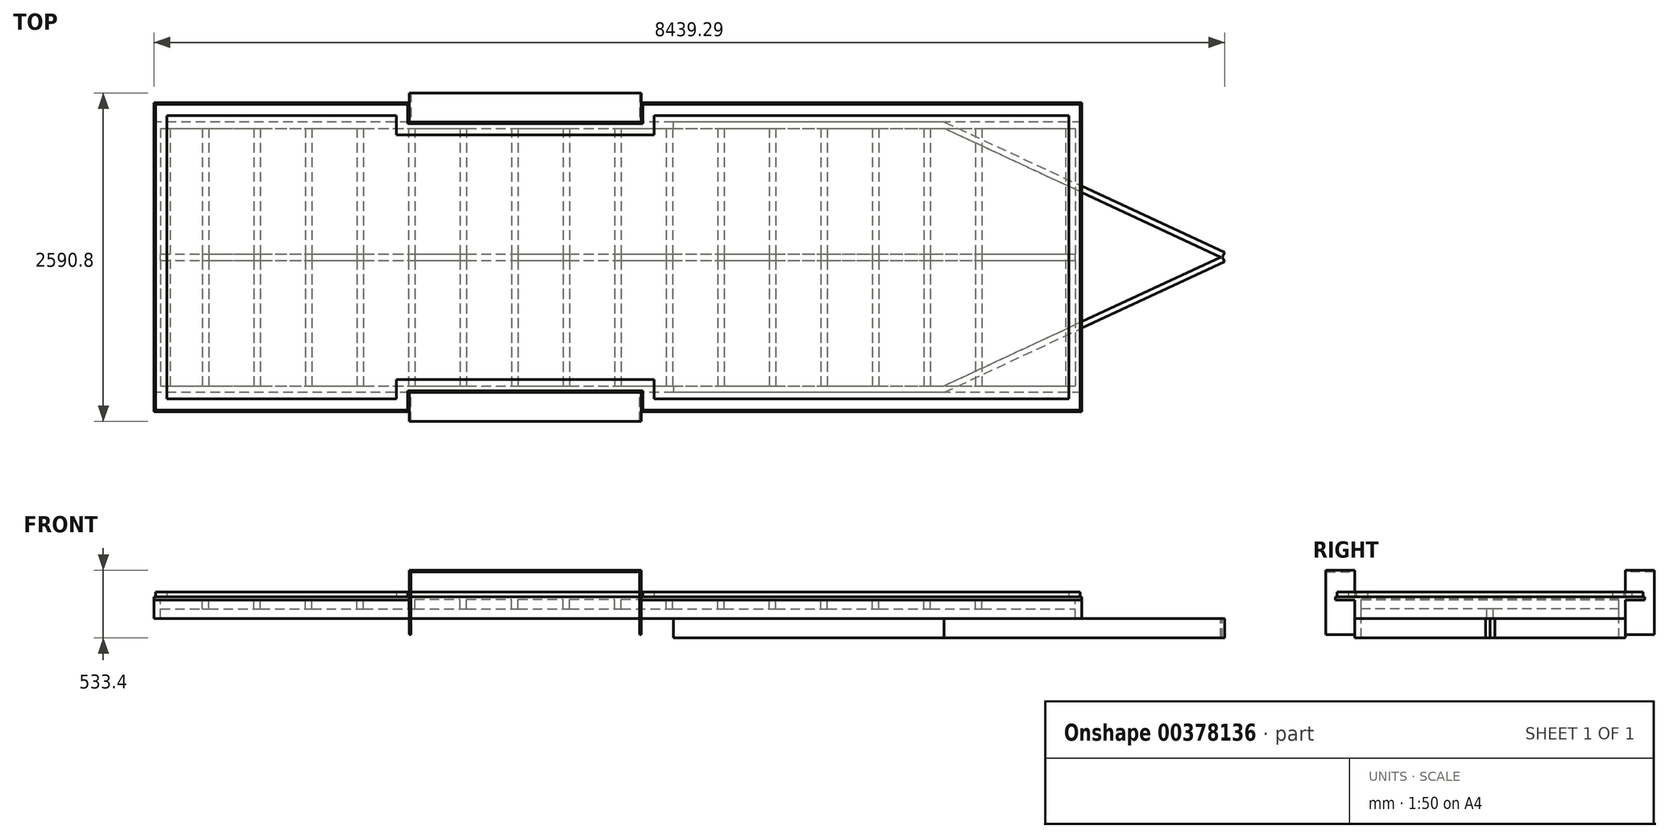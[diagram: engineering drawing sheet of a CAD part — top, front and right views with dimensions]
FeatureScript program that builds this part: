
annotation { "Feature Type Name" : "Feature", "Feature Type Description" : "" }
export const myFeature = defineFeature(function(context is Context, id is Id, definition is map)
    precondition{}
    {
        {
            var Q0;
            Q0=qCreatedBy(makeId("Top.planeOp"),FACE);
            var sketch = newSketch(context, id + "F0", { "sketchPlane" : qUnion([Q0])});
            skLineSegment(sketch, "E0.bottom", {"start": v(3657.6, 1219.2) * mm, "end": v(184.15, 1219.2) * mm});
            skLineSegment(sketch, "E0.top", {"start": v(3657.6, -1219.2) * mm, "end": v(184.15, -1219.2) * mm});
            skLineSegment(sketch, "E0.left", {"start": v(3657.6, 1219.2) * mm, "end": v(3657.6, -1219.2) * mm});
            skLineSegment(sketch, "E0.right", {"start": v(-3657.6, 1219.2) * mm, "end": v(-3657.6, -1219.2) * mm});
            skPoint(sketch, "E0.middle", {"position": v(0, 0) * mm});
            skLineSegment(sketch, "E1.bottom", {"start": v(3657.6, 1066.8) * mm, "end": v(-3657.6, 1066.8) * mm});
            skLineSegment(sketch, "E1.top", {"start": v(3657.6, -1066.8) * mm, "end": v(-3657.6, -1066.8) * mm});
            skLineSegment(sketch, "E2.bottom", {"start": v(-3606.8, 1016) * mm, "end": v(3606.8, 1016) * mm});
            skLineSegment(sketch, "E2.top", {"start": v(-3606.8, -1016) * mm, "end": v(3606.8, -1016) * mm});
            skLineSegment(sketch, "E2.left", {"start": v(-3606.8, 1016) * mm, "end": v(-3606.8, -1016) * mm});
            skLineSegment(sketch, "E2.right", {"start": v(3606.8, 1016) * mm, "end": v(3606.8, -1016) * mm});
            skLineSegment(sketch, "E3", {"start": v(-3530.6, 1016) * mm, "end": v(-3530.6, -1016) * mm});
            skLineSegment(sketch, "E4", {"start": v(3530.6, 1016) * mm, "end": v(3530.6, -1016) * mm});
            skLineSegment(sketch, "E5", {"start": v(3251.2, 1016) * mm, "end": v(3251.2, -1016) * mm, "construction": true});
            skPoint(sketch, "E6", {"position": v(3251.2, 0) * mm});
            skLineSegment(sketch, "E7.bottom", {"start": v(3276.6, 1016) * mm, "end": v(3225.8, 1016) * mm});
            skLineSegment(sketch, "E7.top", {"start": v(3276.6, -1016) * mm, "end": v(3225.8, -1016) * mm});
            skLineSegment(sketch, "E7.left", {"start": v(3276.6, 1016) * mm, "end": v(3276.6, -1016) * mm});
            skLineSegment(sketch, "E7.right", {"start": v(3225.8, 1016) * mm, "end": v(3225.8, -1016) * mm});
            skLineSegment(sketch, "E8.1.0.0", {"start": v(2819.4, 1016) * mm, "end": v(2819.4, -1016) * mm});
            skLineSegment(sketch, "E8.1.0.1", {"start": v(2870.2, 1016) * mm, "end": v(2870.2, -1016) * mm});
            skLineSegment(sketch, "E8.2.0.0", {"start": v(2413, 1016) * mm, "end": v(2413, -1016) * mm});
            skLineSegment(sketch, "E8.2.0.1", {"start": v(2463.8, 1016) * mm, "end": v(2463.8, -1016) * mm});
            skLineSegment(sketch, "E8.3.0.0", {"start": v(2006.6, 1016) * mm, "end": v(2006.6, -1016) * mm});
            skLineSegment(sketch, "E8.3.0.1", {"start": v(2057.4, 1016) * mm, "end": v(2057.4, -1016) * mm});
            skLineSegment(sketch, "E8.4.0.0", {"start": v(1600.2, 1016) * mm, "end": v(1600.2, -1016) * mm});
            skLineSegment(sketch, "E8.4.0.1", {"start": v(1651, 1016) * mm, "end": v(1651, -1016) * mm});
            skLineSegment(sketch, "E8.5.0.0", {"start": v(1193.8, 1016) * mm, "end": v(1193.8, -1016) * mm});
            skLineSegment(sketch, "E8.5.0.1", {"start": v(1244.6, 1016) * mm, "end": v(1244.6, -1016) * mm});
            skLineSegment(sketch, "E8.6.0.0", {"start": v(787.4, 1016) * mm, "end": v(787.4, -1016) * mm});
            skLineSegment(sketch, "E8.6.0.1", {"start": v(838.2, 1016) * mm, "end": v(838.2, -1016) * mm});
            skLineSegment(sketch, "E8.7.0.0", {"start": v(381, 1016) * mm, "end": v(381, -1016) * mm});
            skLineSegment(sketch, "E8.7.0.1", {"start": v(431.8, 1016) * mm, "end": v(431.8, -1016) * mm});
            skLineSegment(sketch, "E8.8.0.0", {"start": v(-25.4, 1016) * mm, "end": v(-25.4, -1016) * mm});
            skLineSegment(sketch, "E8.8.0.1", {"start": v(25.4, 1016) * mm, "end": v(25.4, -1016) * mm});
            skLineSegment(sketch, "E8.9.0.0", {"start": v(-431.8, 1016) * mm, "end": v(-431.8, -1016) * mm});
            skLineSegment(sketch, "E8.9.0.1", {"start": v(-381, 1016) * mm, "end": v(-381, -1016) * mm});
            skLineSegment(sketch, "E8.10.0.0", {"start": v(-838.2, 1016) * mm, "end": v(-838.2, -1016) * mm});
            skLineSegment(sketch, "E8.10.0.1", {"start": v(-787.4, 1016) * mm, "end": v(-787.4, -1016) * mm});
            skLineSegment(sketch, "E8.11.0.0", {"start": v(-1244.6, 1016) * mm, "end": v(-1244.6, -1016) * mm});
            skLineSegment(sketch, "E8.11.0.1", {"start": v(-1193.8, 1016) * mm, "end": v(-1193.8, -1016) * mm});
            skLineSegment(sketch, "E8.12.0.0", {"start": v(-1651, 1016) * mm, "end": v(-1651, -1016) * mm});
            skLineSegment(sketch, "E8.12.0.1", {"start": v(-1600.2, 1016) * mm, "end": v(-1600.2, -1016) * mm});
            skLineSegment(sketch, "E8.13.0.0", {"start": v(-2057.4, 1016) * mm, "end": v(-2057.4, -1016) * mm});
            skLineSegment(sketch, "E8.13.0.1", {"start": v(-2006.6, 1016) * mm, "end": v(-2006.6, -1016) * mm});
            skLineSegment(sketch, "E8.14.0.0", {"start": v(-2463.8, 1016) * mm, "end": v(-2463.8, -1016) * mm});
            skLineSegment(sketch, "E8.14.0.1", {"start": v(-2413, 1016) * mm, "end": v(-2413, -1016) * mm});
            skLineSegment(sketch, "E8.15.0.0", {"start": v(-2870.2, 1016) * mm, "end": v(-2870.2, -1016) * mm});
            skLineSegment(sketch, "E8.15.0.1", {"start": v(-2819.4, 1016) * mm, "end": v(-2819.4, -1016) * mm});
            skLineSegment(sketch, "E8.16.0.0", {"start": v(-3276.6, 1016) * mm, "end": v(-3276.6, -1016) * mm});
            skLineSegment(sketch, "E8.16.0.1", {"start": v(-3225.8, 1016) * mm, "end": v(-3225.8, -1016) * mm});
            skLineSegment(sketch, "E8.direction1", {"start": v(3225.8, -1016) * mm, "end": v(2819.4, -1016) * mm, "construction": true});
            skLineSegment(sketch, "E9", {"start": v(-1644.65, 1219.2) * mm, "end": v(-1644.65, 1066.8) * mm});
            skLineSegment(sketch, "E10", {"start": v(184.15, 1219.2) * mm, "end": v(184.15, 1066.8) * mm});
            skLineSegment(sketch, "E11", {"start": v(184.15, -1066.8) * mm, "end": v(184.15, -1219.2) * mm});
            skLineSegment(sketch, "E12", {"start": v(-1644.65, -1066.8) * mm, "end": v(-1644.65, -1219.2) * mm});
            skLineSegment(sketch, "E13.trimOffspring", {"start": v(-1644.65, 1219.2) * mm, "end": v(-3657.6, 1219.2) * mm});
            skLineSegment(sketch, "E14.trimOffspring", {"start": v(-1644.65, -1219.2) * mm, "end": v(-3657.6, -1219.2) * mm});
            skSolve(sketch);
        }
        {
            var Q0;
            {var subQ4=sQuery(id+"F0.wireOp",EDGE,"E12");Q0=makeQuery(id+"F0.imprint","IMPRINT",FACE,{"disambiguationData":[TD([[makeQuery(id+"F0.imprint","IMPRINT",EDGE,{"derivedFrom":subQ4}),-1.0]])]});}
            var Q1;
            {var subQ0=sQuery(id+"F0.wireOp",EDGE,"E2.left");Q1=makeQuery(id+"F0.imprint","IMPRINT",FACE,{"disambiguationData":[TD([[makeQuery(id+"F0.imprint","IMPRINT",EDGE,{"derivedFrom":subQ0}),1.0]])]});}
            var Q2;
            {var subQ4=sQuery(id+"F0.wireOp",EDGE,"E9");Q2=makeQuery(id+"F0.imprint","IMPRINT",FACE,{"disambiguationData":[TD([[makeQuery(id+"F0.imprint","IMPRINT",EDGE,{"derivedFrom":subQ4}),-1.0]])]});}
            var Q3;
            {var subQ0=sQuery(id+"F0.wireOp",EDGE,"E0.bottom");Q3=makeQuery(id+"F0.imprint","IMPRINT",FACE,{"disambiguationData":[TD([[makeQuery(id+"F0.imprint","IMPRINT",EDGE,{"derivedFrom":subQ0}),1.0]])]});}
            var Q4;
            {var subQ0=sQuery(id+"F0.wireOp",EDGE,"E2.right");Q4=makeQuery(id+"F0.imprint","IMPRINT",FACE,{"disambiguationData":[TD([[makeQuery(id+"F0.imprint","IMPRINT",EDGE,{"derivedFrom":subQ0}),-1.0]])]});}
            var Q5;
            {var subQ0=sQuery(id+"F0.wireOp",EDGE,"E0.top");Q5=makeQuery(id+"F0.imprint","IMPRINT",FACE,{"disambiguationData":[TD([[makeQuery(id+"F0.imprint","IMPRINT",EDGE,{"derivedFrom":subQ0}),-1.0]])]});}
            extrude(context, id + "F1", {"entities" : qUnion([Q0, Q1, Q2, Q3, Q4, Q5]), "oppositeDirection" : true, "depth" : 6.35 * mm});
        }
        {
            var Q0;
            {var subQ64=sQuery(id+"F0.wireOp",EDGE,"E2.left");Q0=makeQuery(id+"F0.imprint","IMPRINT",FACE,{"disambiguationData":[TD([[makeQuery(id+"F0.imprint","IMPRINT",EDGE,{"derivedFrom":subQ64}),-1.0]])]});}
            extrude(context, id + "F2", {"entities" : qUnion([Q0]), "oppositeDirection" : true, "depth" : 152.4 * mm});
        }
        {
            var Q0;
            {var subQ0=sQuery(id+"F0.wireOp",EDGE,"E8.16.0.0");Q0=makeQuery(id+"F0.imprint","IMPRINT",FACE,{"disambiguationData":[TD([[makeQuery(id+"F0.imprint","IMPRINT",EDGE,{"derivedFrom":subQ0}),1.0]])]});}
            var Q1;
            {var subQ0=sQuery(id+"F0.wireOp",EDGE,"E8.15.0.0");Q1=makeQuery(id+"F0.imprint","IMPRINT",FACE,{"disambiguationData":[TD([[makeQuery(id+"F0.imprint","IMPRINT",EDGE,{"derivedFrom":subQ0}),1.0]])]});}
            var Q2;
            {var subQ0=sQuery(id+"F0.wireOp",EDGE,"E8.14.0.0");Q2=makeQuery(id+"F0.imprint","IMPRINT",FACE,{"disambiguationData":[TD([[makeQuery(id+"F0.imprint","IMPRINT",EDGE,{"derivedFrom":subQ0}),1.0]])]});}
            var Q3;
            {var subQ0=sQuery(id+"F0.wireOp",EDGE,"E8.13.0.0");Q3=makeQuery(id+"F0.imprint","IMPRINT",FACE,{"disambiguationData":[TD([[makeQuery(id+"F0.imprint","IMPRINT",EDGE,{"derivedFrom":subQ0}),1.0]])]});}
            var Q4;
            {var subQ0=sQuery(id+"F0.wireOp",EDGE,"E8.12.0.0");Q4=makeQuery(id+"F0.imprint","IMPRINT",FACE,{"disambiguationData":[TD([[makeQuery(id+"F0.imprint","IMPRINT",EDGE,{"derivedFrom":subQ0}),1.0]])]});}
            var Q5;
            {var subQ0=sQuery(id+"F0.wireOp",EDGE,"E8.11.0.0");Q5=makeQuery(id+"F0.imprint","IMPRINT",FACE,{"disambiguationData":[TD([[makeQuery(id+"F0.imprint","IMPRINT",EDGE,{"derivedFrom":subQ0}),1.0]])]});}
            var Q6;
            {var subQ0=sQuery(id+"F0.wireOp",EDGE,"E8.10.0.0");Q6=makeQuery(id+"F0.imprint","IMPRINT",FACE,{"disambiguationData":[TD([[makeQuery(id+"F0.imprint","IMPRINT",EDGE,{"derivedFrom":subQ0}),1.0]])]});}
            var Q7;
            {var subQ0=sQuery(id+"F0.wireOp",EDGE,"E8.9.0.0");Q7=makeQuery(id+"F0.imprint","IMPRINT",FACE,{"disambiguationData":[TD([[makeQuery(id+"F0.imprint","IMPRINT",EDGE,{"derivedFrom":subQ0}),1.0]])]});}
            var Q8;
            {var subQ0=sQuery(id+"F0.wireOp",EDGE,"E8.8.0.0");Q8=makeQuery(id+"F0.imprint","IMPRINT",FACE,{"disambiguationData":[TD([[makeQuery(id+"F0.imprint","IMPRINT",EDGE,{"derivedFrom":subQ0}),1.0]])]});}
            var Q9;
            {var subQ0=sQuery(id+"F0.wireOp",EDGE,"E8.7.0.0");Q9=makeQuery(id+"F0.imprint","IMPRINT",FACE,{"disambiguationData":[TD([[makeQuery(id+"F0.imprint","IMPRINT",EDGE,{"derivedFrom":subQ0}),1.0]])]});}
            var Q10;
            {var subQ0=sQuery(id+"F0.wireOp",EDGE,"E8.6.0.0");Q10=makeQuery(id+"F0.imprint","IMPRINT",FACE,{"disambiguationData":[TD([[makeQuery(id+"F0.imprint","IMPRINT",EDGE,{"derivedFrom":subQ0}),1.0]])]});}
            var Q11;
            {var subQ0=sQuery(id+"F0.wireOp",EDGE,"E8.5.0.0");Q11=makeQuery(id+"F0.imprint","IMPRINT",FACE,{"disambiguationData":[TD([[makeQuery(id+"F0.imprint","IMPRINT",EDGE,{"derivedFrom":subQ0}),1.0]])]});}
            var Q12;
            {var subQ0=sQuery(id+"F0.wireOp",EDGE,"E8.4.0.0");Q12=makeQuery(id+"F0.imprint","IMPRINT",FACE,{"disambiguationData":[TD([[makeQuery(id+"F0.imprint","IMPRINT",EDGE,{"derivedFrom":subQ0}),1.0]])]});}
            var Q13;
            {var subQ0=sQuery(id+"F0.wireOp",EDGE,"E8.3.0.0");Q13=makeQuery(id+"F0.imprint","IMPRINT",FACE,{"disambiguationData":[TD([[makeQuery(id+"F0.imprint","IMPRINT",EDGE,{"derivedFrom":subQ0}),1.0]])]});}
            var Q14;
            {var subQ0=sQuery(id+"F0.wireOp",EDGE,"E8.2.0.0");Q14=makeQuery(id+"F0.imprint","IMPRINT",FACE,{"disambiguationData":[TD([[makeQuery(id+"F0.imprint","IMPRINT",EDGE,{"derivedFrom":subQ0}),1.0]])]});}
            var Q15;
            {var subQ0=sQuery(id+"F0.wireOp",EDGE,"E8.1.0.0");Q15=makeQuery(id+"F0.imprint","IMPRINT",FACE,{"disambiguationData":[TD([[makeQuery(id+"F0.imprint","IMPRINT",EDGE,{"derivedFrom":subQ0}),1.0]])]});}
            var Q16;
            Q16=makeQuery(id+"F0.imprint","IMPRINT",FACE,{"disambiguationData":[TD([[makeQuery(id+"F0.imprint","IMPRINT",EDGE,{"derivedFrom":sQuery(id+"F0.wireOp",EDGE,"E7.bottom")}),1.0]])]});
            extrude(context, id + "F3", {"entities" : qUnion([Q0, Q1, Q2, Q3, Q4, Q5, Q6, Q7, Q8, Q9, Q10, Q11, Q12, Q13, Q14, Q15, Q16]), "oppositeDirection" : true, "depth" : 76.2 * mm});
        }
        {
            var Q0;
            Q0=makeQuery(id+"F3.opExtrude","CAP_FACE",FACE,{"disambiguationData":[OSD([sQuery(id+"F0.wireOp",EDGE,"E2.bottom"),sQuery(id+"F0.wireOp",EDGE,"E2.top"),sQuery(id+"F0.wireOp",EDGE,"E8.10.0.0"),sQuery(id+"F0.wireOp",EDGE,"E8.10.0.1")])],"isStart":false});
            var sketch = newSketch(context, id + "F4", { "sketchPlane" : qUnion([Q0])});
            skLineSegment(sketch, "E15.bottom", {"start": v(-3606.8, 25.4) * mm, "end": v(3606.8, 25.4) * mm});
            skLineSegment(sketch, "E15.top", {"start": v(-3606.8, -25.4) * mm, "end": v(3606.8, -25.4) * mm});
            skLineSegment(sketch, "E15.left", {"start": v(-3606.8, 25.4) * mm, "end": v(-3606.8, -25.4) * mm});
            skLineSegment(sketch, "E15.right", {"start": v(3606.8, 25.4) * mm, "end": v(3606.8, -25.4) * mm});
            skPoint(sketch, "E15.middle", {"position": v(0, 0) * mm});
            skSolve(sketch);
        }
        {
            var Q0;
            {var subQ0=sQuery(id+"F4.wireOp",EDGE,"E15.left");Q0=makeQuery(id+"F4.imprint","IMPRINT",FACE,{"disambiguationData":[TD([[makeQuery(id+"F4.imprint","IMPRINT",EDGE,{"derivedFrom":subQ0}),1.0]])]});}
            var Q1;
            {var subQ0=sQuery(id+"F4.wireOp",EDGE,"E15.right");Q1=makeQuery(id+"F4.imprint","IMPRINT",FACE,{"disambiguationData":[TD([[makeQuery(id+"F4.imprint","IMPRINT",EDGE,{"derivedFrom":subQ0}),-1.0]])]});}
            var Q2;
            {var subQ0=sQuery(id+"F4.wireOp",EDGE,"E15.bottom");var subQ1=makeQuery(id+"F3.opExtrude","CAP_EDGE",EDGE,{"disambiguationData":[OSD([sQuery(id+"F0.wireOp",EDGE,"E8.10.0.0")])],"isStart":false});var subQ2=makeQuery(id+"F4.imprint","INTERSECT",VERTEX,{"derivedFrom":[subQ1,subQ0]});Q2=makeQuery(id+"F4.imprint","IMPRINT",FACE,{"disambiguationData":[TD([[makeQuery(id+"F4.imprint","IMPRINT",EDGE,{"disambiguationData":[TD([[subQ2,-1.0]])],"derivedFrom":subQ0}),-1.0]])]});}
            extrude(context, id + "F5", {"entities" : qUnion([Q0, Q1, Q2]), "operationType" : NewBodyOperationType.ADD, "depth" : 76.2 * mm});
        }
        {
            var Q0;
            Q0=makeQuery(id+"F2.opExtrude","SWEPT_FACE",FACE,{"disambiguationData":[OSD([sQuery(id+"F0.wireOp",EDGE,"E1.top")])]});
            var sketch = newSketch(context, id + "F6", { "sketchPlane" : qUnion([Q0])});
            skLineSegment(sketch, "E16", {"start": v(-1644.65, -279.4) * mm, "end": v(-1644.65, 228.6) * mm});
            skLineSegment(sketch, "E17", {"start": v(-1644.65, 228.6) * mm, "end": v(184.15, 228.6) * mm});
            skLineSegment(sketch, "E18", {"start": v(184.15, 228.6) * mm, "end": v(184.15, -279.4) * mm});
            skLineSegment(sketch, "E19.0", {"start": v(171.45, 215.9) * mm, "end": v(171.45, -279.4) * mm});
            skLineSegment(sketch, "E19.1", {"start": v(-1631.95, 215.9) * mm, "end": v(171.45, 215.9) * mm});
            skLineSegment(sketch, "E19.2", {"start": v(-1631.95, -279.4) * mm, "end": v(-1631.95, 215.9) * mm});
            skLineSegment(sketch, "E20", {"start": v(-1644.65, -279.4) * mm, "end": v(-1631.95, -279.4) * mm});
            skLineSegment(sketch, "E21", {"start": v(171.45, -279.4) * mm, "end": v(184.15, -279.4) * mm});
            skSolve(sketch);
        }
        {
            var Q0;
            Q0 = qSketchRegion(id + "F6", true);
            extrude(context, id + "F7", {"entities" : qUnion([Q0]), "depth" : 228.6 * mm});
        }
        {
            var Q0;
            Q0=makeQuery(id+"F7.opExtrude","SWEPT_BODY",BODY,{"disambiguationData":[OSD([sQuery(id+"F6.wireOp",EDGE,"E16"),sQuery(id+"F6.wireOp",EDGE,"E17"),sQuery(id+"F6.wireOp",EDGE,"E18"),sQuery(id+"F6.wireOp",EDGE,"E19.0"),sQuery(id+"F6.wireOp",EDGE,"E19.1"),sQuery(id+"F6.wireOp",EDGE,"E19.2"),sQuery(id+"F6.wireOp",EDGE,"E20"),sQuery(id+"F6.wireOp",EDGE,"E21")])]});
            var Q1;
            Q1=qCreatedBy(makeId("Front.planeOp"),FACE);
            mirror(context, id + "F8", {"operationType" : NewBodyOperationType.ADD, "entities" : qUnion([Q0]), "mirrorPlane" : qUnion([Q1])});
        }
        {
            var Q0;
            Q0=makeQuery(id+"F5.boolean.opBoolean","MERGE",FACE,{"derivedFrom":[makeQuery(id+"F2.opExtrude","CAP_FACE",FACE,{"disambiguationData":[OSD([sQuery(id+"F0.wireOp",EDGE,"E0.left"),sQuery(id+"F0.wireOp",EDGE,"E0.right"),sQuery(id+"F0.wireOp",EDGE,"E1.bottom"),sQuery(id+"F0.wireOp",EDGE,"E1.top"),sQuery(id+"F0.wireOp",EDGE,"E2.bottom"),sQuery(id+"F0.wireOp",EDGE,"E2.top"),sQuery(id+"F0.wireOp",EDGE,"E2.left"),sQuery(id+"F0.wireOp",EDGE,"E2.right"),sQuery(id+"F0.wireOp",EDGE,"E7.bottom"),sQuery(id+"F0.wireOp",EDGE,"E7.top")])],"isStart":false}),makeQuery(id+"F5.opExtrude","CAP_FACE",FACE,{"disambiguationData":[OSD([sQuery(id+"F4.wireOp",EDGE,"E15.bottom"),sQuery(id+"F4.wireOp",EDGE,"E15.top"),sQuery(id+"F4.wireOp",EDGE,"E15.left"),sQuery(id+"F4.wireOp",EDGE,"E15.right")])],"isStart":false})]});
            var sketch = newSketch(context, id + "F9", { "sketchPlane" : qUnion([Q0])});
            skLineSegment(sketch, "E22", {"start": v(438.15, 1016) * mm, "end": v(438.15, 1066.8) * mm});
            skLineSegment(sketch, "E23", {"start": v(438.15, 1066.8) * mm, "end": v(2571.75, 1066.8) * mm});
            skLineSegment(sketch, "E24", {"start": v(2571.75, 1066.8) * mm, "end": v(4781.7, 36.29) * mm});
            skLineSegment(sketch, "E25", {"start": v(4781.7, 36.29) * mm, "end": v(4764.77, 0) * mm});
            skLineSegment(sketch, "E26", {"start": v(2571.75, 1016) * mm, "end": v(438.15, 1016) * mm});
            skLineSegment(sketch, "E27", {"start": v(0, 0) * mm, "end": v(5571.54, 0) * mm, "construction": true});
            skLineSegment(sketch, "E28.MirrorCS", {"start": v(438.15, -1066.8) * mm, "end": v(2571.75, -1066.8) * mm});
            skLineSegment(sketch, "E29.MirrorCS", {"start": v(2571.75, -1066.8) * mm, "end": v(4781.7, -36.29) * mm});
            skLineSegment(sketch, "E30.MirrorCS", {"start": v(2571.75, -1016) * mm, "end": v(438.15, -1016) * mm});
            skLineSegment(sketch, "E31.MirrorCS", {"start": v(438.15, -1016) * mm, "end": v(438.15, -1066.8) * mm});
            skLineSegment(sketch, "E32.MirrorCS", {"start": v(4781.7, -36.29) * mm, "end": v(4764.77, 0) * mm});
            skPoint(sketch, "E33", {"position": v(4764.77, 0) * mm});
            skLineSegment(sketch, "E34", {"start": v(4750.57, 0) * mm, "end": v(2571.75, -1016) * mm});
            skLineSegment(sketch, "E35", {"start": v(4750.57, 0) * mm, "end": v(2571.75, 1016) * mm});
            skPoint(sketch, "E36.start.orphan", {"position": v(4762.23, -5.44) * mm});
            skPoint(sketch, "E37.MirrorCS.start.orphan", {"position": v(4762.23, 5.44) * mm});
            skSolve(sketch);
        }
        {
            var Q0;
            {var subQ0=sQuery(id+"F9.wireOp",EDGE,"E24");var subQ1=sQuery(id+"F0.wireOp",EDGE,"E7.top");var subQ2=sQuery(id+"F0.wireOp",EDGE,"E2.top");var subQ3=makeQuery(id+"F2.opExtrude","CAP_EDGE",EDGE,{"disambiguationData":[OSD([subQ2,subQ1])],"isStart":false});var subQ4=makeQuery(id+"F9.imprint","INTERSECT",VERTEX,{"derivedFrom":[subQ3,subQ0]});Q0=makeQuery(id+"F9.imprint","IMPRINT",FACE,{"disambiguationData":[TD([[makeQuery(id+"F9.imprint","IMPRINT",EDGE,{"disambiguationData":[TD([[subQ4,1.0]])],"derivedFrom":subQ3}),-1.0]])]});}
            var Q1;
            {var subQ5=sQuery(id+"F9.wireOp",EDGE,"E24");var subQ9=sQuery(id+"F9.wireOp",EDGE,"E25");var subQ10=makeQuery(id+"F9.imprint","INTERSECT",VERTEX,{"derivedFrom":[subQ5,subQ9]});Q1=makeQuery(id+"F9.imprint","IMPRINT",FACE,{"disambiguationData":[TD([[makeQuery(id+"F9.imprint","IMPRINT",EDGE,{"disambiguationData":[TD([[subQ10,1.0]])],"derivedFrom":subQ5}),-1.0]])]});}
            var Q2;
            {var subQ0=sQuery(id+"F9.wireOp",EDGE,"E24");var subQ1=sQuery(id+"F0.wireOp",EDGE,"E0.left");var subQ2=makeQuery(id+"F2.opExtrude","CAP_EDGE",EDGE,{"disambiguationData":[OSD([subQ1])],"isStart":false});var subQ3=makeQuery(id+"F9.imprint","INTERSECT",VERTEX,{"derivedFrom":[subQ2,subQ0]});Q2=makeQuery(id+"F9.imprint","IMPRINT",FACE,{"disambiguationData":[TD([[makeQuery(id+"F9.imprint","IMPRINT",EDGE,{"disambiguationData":[TD([[subQ3,1.0]])],"derivedFrom":subQ2}),1.0]])]});}
            var Q3;
            {var subQ6=sQuery(id+"F9.wireOp",EDGE,"E36");var subQ9=sQuery(id+"F9.wireOp",EDGE,"E25");var subQ10=makeQuery(id+"F9.imprint","INTERSECT",VERTEX,{"derivedFrom":[subQ9,subQ6]});Q3=makeQuery(id+"F9.imprint","IMPRINT",FACE,{"disambiguationData":[TD([[makeQuery(id+"F9.imprint","IMPRINT",EDGE,{"disambiguationData":[TD([[subQ10,1.0]])],"derivedFrom":subQ9}),1.0]])]});}
            var Q4;
            {var subQ1=sQuery(id+"F0.wireOp",EDGE,"E0.left");var subQ2=makeQuery(id+"F2.opExtrude","CAP_EDGE",EDGE,{"disambiguationData":[OSD([subQ1])],"isStart":false});var subQ10=sQuery(id+"F9.wireOp",EDGE,"E29.MirrorCS");var subQ11=makeQuery(id+"F9.imprint","INTERSECT",VERTEX,{"derivedFrom":[subQ2,subQ10]});Q4=makeQuery(id+"F9.imprint","IMPRINT",FACE,{"disambiguationData":[TD([[makeQuery(id+"F9.imprint","IMPRINT",EDGE,{"disambiguationData":[TD([[subQ11,-1.0]])],"derivedFrom":subQ2}),1.0]])]});}
            var Q5;
            {var subQ1=sQuery(id+"F0.wireOp",EDGE,"E7.bottom");var subQ2=sQuery(id+"F0.wireOp",EDGE,"E2.bottom");var subQ3=makeQuery(id+"F2.opExtrude","CAP_EDGE",EDGE,{"disambiguationData":[OSD([subQ2,subQ1])],"isStart":false});var subQ9=sQuery(id+"F9.wireOp",EDGE,"E29.MirrorCS");var subQ10=makeQuery(id+"F9.imprint","INTERSECT",VERTEX,{"derivedFrom":[subQ3,subQ9]});Q5=makeQuery(id+"F9.imprint","IMPRINT",FACE,{"disambiguationData":[TD([[makeQuery(id+"F9.imprint","IMPRINT",EDGE,{"disambiguationData":[TD([[subQ10,1.0]])],"derivedFrom":subQ3}),1.0]])]});}
            var Q6;
            {var subQ0=sQuery(id+"F9.wireOp",EDGE,"E28.MirrorCS");Q6=makeQuery(id+"F9.imprint","IMPRINT",FACE,{"disambiguationData":[TD([[makeQuery(id+"F9.imprint","IMPRINT",EDGE,{"derivedFrom":subQ0}),-1.0]])]});}
            var Q7;
            Q7=makeQuery(id+"F9.imprint","IMPRINT",FACE,{"disambiguationData":[TD([[makeQuery(id+"F9.imprint","IMPRINT",EDGE,{"derivedFrom":sQuery(id+"F9.wireOp",EDGE,"E22")}),-1.0]])]});
            extrude(context, id + "F10", {"entities" : qUnion([Q0, Q1, Q2, Q3, Q4, Q5, Q6, Q7]), "depth" : 152.4 * mm});
        }
        {
            var Q0;
            {var subQ0=sQuery(id+"F0.wireOp",EDGE,"E0.bottom");Q0=makeQuery(id+"F0.imprint","IMPRINT",FACE,{"disambiguationData":[TD([[makeQuery(id+"F0.imprint","IMPRINT",EDGE,{"derivedFrom":subQ0}),1.0]])]});}
            var sketch = newSketch(context, id + "F11", { "sketchPlane" : qUnion([Q0])});
            skLineSegment(sketch, "E38.bottom", {"start": v(3657.6, -1219.2) * mm, "end": v(2438.4, -1219.2) * mm});
            skLineSegment(sketch, "E38.top", {"start": v(3657.6, 1219.2) * mm, "end": v(2438.4, 1219.2) * mm});
            skLineSegment(sketch, "E38.left", {"start": v(3657.6, -1219.2) * mm, "end": v(3657.6, 1219.2) * mm});
            skLineSegment(sketch, "E38.right", {"start": v(2438.4, -1219.2) * mm, "end": v(2438.4, 1219.2) * mm});
            skLineSegment(sketch, "E39.bottom", {"start": v(2438.4, -1219.2) * mm, "end": v(1219.2, -1219.2) * mm});
            skLineSegment(sketch, "E39.top", {"start": v(2438.4, 1219.2) * mm, "end": v(1219.2, 1219.2) * mm});
            skLineSegment(sketch, "E39.right", {"start": v(1219.2, -1219.2) * mm, "end": v(1219.2, 1219.2) * mm});
            skLineSegment(sketch, "E40", {"start": v(1219.2, 1219.2) * mm, "end": v(184.15, 1219.2) * mm});
            skLineSegment(sketch, "E41", {"start": v(184.15, 1219.2) * mm, "end": v(184.15, 1066.8) * mm});
            skLineSegment(sketch, "E42", {"start": v(184.15, 1066.8) * mm, "end": v(0, 1066.8) * mm});
            skLineSegment(sketch, "E43", {"start": v(0, 1066.8) * mm, "end": v(0, -1066.8) * mm});
            skLineSegment(sketch, "E44", {"start": v(0, -1066.8) * mm, "end": v(184.15, -1066.8) * mm});
            skLineSegment(sketch, "E45", {"start": v(184.15, -1066.8) * mm, "end": v(184.15, -1219.2) * mm});
            skLineSegment(sketch, "E46", {"start": v(184.15, -1219.2) * mm, "end": v(1219.2, -1219.2) * mm});
            skLineSegment(sketch, "E47.bottom", {"start": v(0, -1066.8) * mm, "end": v(-1219.2, -1066.8) * mm});
            skLineSegment(sketch, "E47.top", {"start": v(0, 1066.8) * mm, "end": v(-1219.2, 1066.8) * mm});
            skLineSegment(sketch, "E47.left", {"start": v(0, -1066.8) * mm, "end": v(0, 1066.8) * mm});
            skLineSegment(sketch, "E47.right", {"start": v(-1219.2, -1066.8) * mm, "end": v(-1219.2, 1066.8) * mm});
            skLineSegment(sketch, "E48", {"start": v(-1219.2, 1066.8) * mm, "end": v(-1644.65, 1066.8) * mm});
            skLineSegment(sketch, "E49", {"start": v(-1644.65, 1066.8) * mm, "end": v(-1644.65, 1219.2) * mm});
            skLineSegment(sketch, "E50", {"start": v(-1644.65, 1219.2) * mm, "end": v(-2438.4, 1219.2) * mm});
            skLineSegment(sketch, "E51", {"start": v(-2438.4, 1219.2) * mm, "end": v(-2438.4, -1219.2) * mm});
            skLineSegment(sketch, "E52", {"start": v(-2438.4, -1219.2) * mm, "end": v(-1644.65, -1219.2) * mm});
            skLineSegment(sketch, "E53", {"start": v(-1644.65, -1219.2) * mm, "end": v(-1644.65, -1066.8) * mm});
            skLineSegment(sketch, "E54", {"start": v(-1644.65, -1066.8) * mm, "end": v(-1219.2, -1066.8) * mm});
            skLineSegment(sketch, "E55.bottom", {"start": v(-2438.4, -1219.2) * mm, "end": v(-3657.6, -1219.2) * mm});
            skLineSegment(sketch, "E55.top", {"start": v(-2438.4, 1219.2) * mm, "end": v(-3657.6, 1219.2) * mm});
            skLineSegment(sketch, "E55.left", {"start": v(-2438.4, -1219.2) * mm, "end": v(-2438.4, 1219.2) * mm});
            skLineSegment(sketch, "E55.right", {"start": v(-3657.6, -1219.2) * mm, "end": v(-3657.6, 1219.2) * mm});
            skSolve(sketch);
        }
        {
            var Q0;
            Q0 = qSketchRegion(id + "F11", true);
            extrude(context, id + "F12", {"entities" : qUnion([Q0]), "operationType" : NewBodyOperationType.ADD, "depth" : 19.05 * mm});
        }
        {
            var Q0;
            Q0=makeQuery(id+"F12.opExtrude","CAP_FACE",FACE,{"disambiguationData":[OSD([sQuery(id+"F11.wireOp",EDGE,"E38.bottom"),sQuery(id+"F11.wireOp",EDGE,"E38.top"),sQuery(id+"F11.wireOp",EDGE,"E38.left"),sQuery(id+"F11.wireOp",EDGE,"E39.bottom"),sQuery(id+"F11.wireOp",EDGE,"E39.top"),sQuery(id+"F11.wireOp",EDGE,"E40"),sQuery(id+"F11.wireOp",EDGE,"E41"),sQuery(id+"F11.wireOp",EDGE,"E42"),sQuery(id+"F11.wireOp",EDGE,"E44"),sQuery(id+"F11.wireOp",EDGE,"E45"),sQuery(id+"F11.wireOp",EDGE,"E46"),sQuery(id+"F11.wireOp",EDGE,"E47.bottom"),sQuery(id+"F11.wireOp",EDGE,"E47.top"),sQuery(id+"F11.wireOp",EDGE,"E48"),sQuery(id+"F11.wireOp",EDGE,"E49"),sQuery(id+"F11.wireOp",EDGE,"E50"),sQuery(id+"F11.wireOp",EDGE,"E52"),sQuery(id+"F11.wireOp",EDGE,"E53"),sQuery(id+"F11.wireOp",EDGE,"E54"),sQuery(id+"F11.wireOp",EDGE,"E55.bottom"),sQuery(id+"F11.wireOp",EDGE,"E55.top"),sQuery(id+"F11.wireOp",EDGE,"E55.right")])],"isStart":false});
            var sketch = newSketch(context, id + "F13", { "sketchPlane" : qUnion([Q0])});
            skLineSegment(sketch, "E56", {"start": v(-3657.6, 1219.2) * mm, "end": v(-1644.65, 1219.2) * mm});
            skLineSegment(sketch, "E57", {"start": v(-1644.65, 1219.2) * mm, "end": v(-1644.65, 1066.8) * mm});
            skLineSegment(sketch, "E58", {"start": v(-1644.65, 1066.8) * mm, "end": v(184.15, 1066.8) * mm});
            skLineSegment(sketch, "E59", {"start": v(184.15, 1066.8) * mm, "end": v(184.15, 1219.2) * mm});
            skLineSegment(sketch, "E60", {"start": v(184.15, 1219.2) * mm, "end": v(3657.6, 1219.2) * mm});
            skLineSegment(sketch, "E61", {"start": v(3657.6, 1219.2) * mm, "end": v(3657.6, -1219.2) * mm});
            skLineSegment(sketch, "E62", {"start": v(3657.6, -1219.2) * mm, "end": v(184.15, -1219.2) * mm});
            skLineSegment(sketch, "E63", {"start": v(184.15, -1219.2) * mm, "end": v(184.15, -1066.8) * mm});
            skLineSegment(sketch, "E64", {"start": v(184.15, -1066.8) * mm, "end": v(-1644.65, -1066.8) * mm});
            skLineSegment(sketch, "E65", {"start": v(-1644.65, -1066.8) * mm, "end": v(-1644.65, -1219.2) * mm});
            skLineSegment(sketch, "E66", {"start": v(-1644.65, -1219.2) * mm, "end": v(-3657.6, -1219.2) * mm});
            skLineSegment(sketch, "E67", {"start": v(-3657.6, -1219.2) * mm, "end": v(-3657.6, 1219.2) * mm});
            skLineSegment(sketch, "E68.0", {"start": v(-3644.9, -1206.5) * mm, "end": v(-3644.9, 1206.5) * mm});
            skLineSegment(sketch, "E68.1", {"start": v(196.85, 1206.5) * mm, "end": v(3644.9, 1206.5) * mm});
            skLineSegment(sketch, "E68.2", {"start": v(196.85, 1054.1) * mm, "end": v(196.85, 1206.5) * mm});
            skLineSegment(sketch, "E68.3", {"start": v(-1657.35, 1054.1) * mm, "end": v(196.85, 1054.1) * mm});
            skLineSegment(sketch, "E68.4", {"start": v(-1657.35, 1206.5) * mm, "end": v(-1657.35, 1054.1) * mm});
            skLineSegment(sketch, "E68.5", {"start": v(3644.9, 1206.5) * mm, "end": v(3644.9, -1206.5) * mm});
            skLineSegment(sketch, "E68.6", {"start": v(-3644.9, 1206.5) * mm, "end": v(-1657.35, 1206.5) * mm});
            skLineSegment(sketch, "E68.7", {"start": v(3644.9, -1206.5) * mm, "end": v(196.85, -1206.5) * mm});
            skLineSegment(sketch, "E68.8", {"start": v(196.85, -1206.5) * mm, "end": v(196.85, -1054.1) * mm});
            skLineSegment(sketch, "E68.9", {"start": v(196.85, -1054.1) * mm, "end": v(-1657.35, -1054.1) * mm});
            skLineSegment(sketch, "E68.10", {"start": v(-1657.35, -1054.1) * mm, "end": v(-1657.35, -1206.5) * mm});
            skLineSegment(sketch, "E68.11", {"start": v(-1657.35, -1206.5) * mm, "end": v(-3644.9, -1206.5) * mm});
            skLineSegment(sketch, "E69.0", {"start": v(-3556, -1117.6) * mm, "end": v(-3556, 1117.6) * mm});
            skLineSegment(sketch, "E69.1", {"start": v(285.75, 1117.6) * mm, "end": v(3556, 1117.6) * mm});
            skLineSegment(sketch, "E69.2", {"start": v(285.75, 965.2) * mm, "end": v(285.75, 1117.6) * mm});
            skLineSegment(sketch, "E69.3", {"start": v(-1746.25, 965.2) * mm, "end": v(285.75, 965.2) * mm});
            skLineSegment(sketch, "E69.4", {"start": v(-1746.25, 1117.6) * mm, "end": v(-1746.25, 965.2) * mm});
            skLineSegment(sketch, "E69.5", {"start": v(3556, 1117.6) * mm, "end": v(3556, -1117.6) * mm});
            skLineSegment(sketch, "E69.6", {"start": v(-3556, 1117.6) * mm, "end": v(-1746.25, 1117.6) * mm});
            skLineSegment(sketch, "E69.7", {"start": v(3556, -1117.6) * mm, "end": v(285.75, -1117.6) * mm});
            skLineSegment(sketch, "E69.8", {"start": v(285.75, -1117.6) * mm, "end": v(285.75, -965.2) * mm});
            skLineSegment(sketch, "E69.9", {"start": v(285.75, -965.2) * mm, "end": v(-1746.25, -965.2) * mm});
            skLineSegment(sketch, "E69.10", {"start": v(-1746.25, -965.2) * mm, "end": v(-1746.25, -1117.6) * mm});
            skLineSegment(sketch, "E69.11", {"start": v(-1746.25, -1117.6) * mm, "end": v(-3556, -1117.6) * mm});
            skSolve(sketch);
        }
        {
            var Q0;
            Q0=makeQuery(id+"F13.imprint","IMPRINT",FACE,{"disambiguationData":[TD([[makeQuery(id+"F13.imprint","IMPRINT",EDGE,{"derivedFrom":sQuery(id+"F13.wireOp",EDGE,"E68.0")}),-1.0]])]});
            extrude(context, id + "F14", {"entities" : qUnion([Q0]), "operationType" : NewBodyOperationType.ADD, "depth" : 38.1 * mm});
        }
    });
